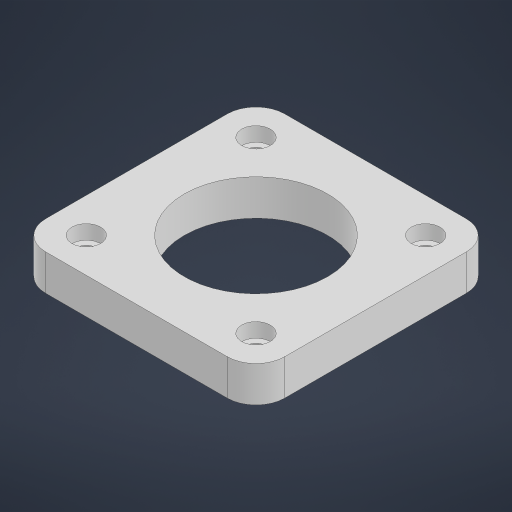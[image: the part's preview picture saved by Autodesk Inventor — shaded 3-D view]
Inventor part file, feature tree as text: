
AUTODESK INVENTOR PART (.ipt)
format: ipt  version: 2024.1 (Build 281209000, 209)  size: 194,560 bytes
history: native  units: mm
features: sketch x1, extrude x1, hole x1, fillet x1
ambient origin geometry x8: Origin, YZ Plane, XZ Plane, XY Plane, X Axis, Y Axis, Z Axis, Center Point
bodies: Solid1 (feature_tree)
feature tree (4):
  sketch  "Sketch1"  dims[d0=100.0mm d1=60.0mm d2=71.0mm d3=15.0mm d4=0.0mm d5=7.0mm d6=7.0mm d7=12.0mm d8=6.0mm d9=90.0deg d10=8.0mm d11=20.594885mm d12=12.0mm d13=100.409163mm]
  extrude  "Extrusion1"  Depth=12.0mm
  hole  "Hole1"  [1 undecoded]
  fillet  "Fillet1"  Radius=15.0mm
note: 1 required parameter value undecoded (feature->parameter linkage not recoverable at this tier; creation-order binding heuristic only, values carry confidence <= 0.55)
